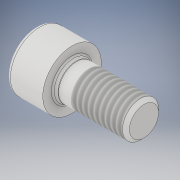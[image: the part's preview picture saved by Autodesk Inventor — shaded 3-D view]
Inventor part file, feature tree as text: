
AUTODESK INVENTOR PART (.ipt)
format: ipt  version: 2019 (Build 230136000, 136)  size: 193,024 bytes
history: native  units: mm
features: other x28, sketch x2, revolve x1, thread x1, extrude x1
ambient origin geometry x8: Origin, YZ Plane, XZ Plane, XY Plane, X Axis, Y Axis, Z Axis, Center Point
bodies: Solid1 (feature_tree)
feature tree (33):
  revolve  "Revolution1"  [1 undecoded]
  thread  "Thread1"  [1 undecoded]
  extrude  "Extrusion1"  [1 undecoded]
  other  "IP1_XY"
  other  "IP1_YZ"
  other  "IP1_ZX"
  other  "IP1_X"
  other  "IP1_Y"
  other  "IP1_Z"
  other  "IP1_Center"
  other  "IP2_XY"
  other  "IP2_YZ"
  other  "IP2_ZX"
  other  "IP2_X"
  other  "IP2_Y"
  other  "IP2_Z"
  other  "IP2_Center"
  other  "IP3_XY"
  other  "IP3_YZ"
  other  "IP3_ZX"
  other  "IP3_X"
  other  "IP3_Y"
  other  "IP3_Z"
  other  "IP3_Center"
  other  "P_GUS_1000_XY"
  other  "P_GUS_1000_YZ"
  other  "P_GUS_1000_ZX"
  other  "P_GUS_1000_X"
  other  "P_GUS_1000_Y"
  other  "P_GUS_1000_Z"
  other  "P_GUS_1000_Center"
  sketch  "Skizze_2"  dims[d5=0.0mm d6=0.0mm d7=0.0mm]
  sketch  "Skizze_1"  dims[d0=360.0deg d1=11.483mm d2=0.0mm d3=8.0mm d4=0.0mm]
note: 3 required parameter values undecoded (feature->parameter linkage not recoverable at this tier; creation-order binding heuristic only, values carry confidence <= 0.55)